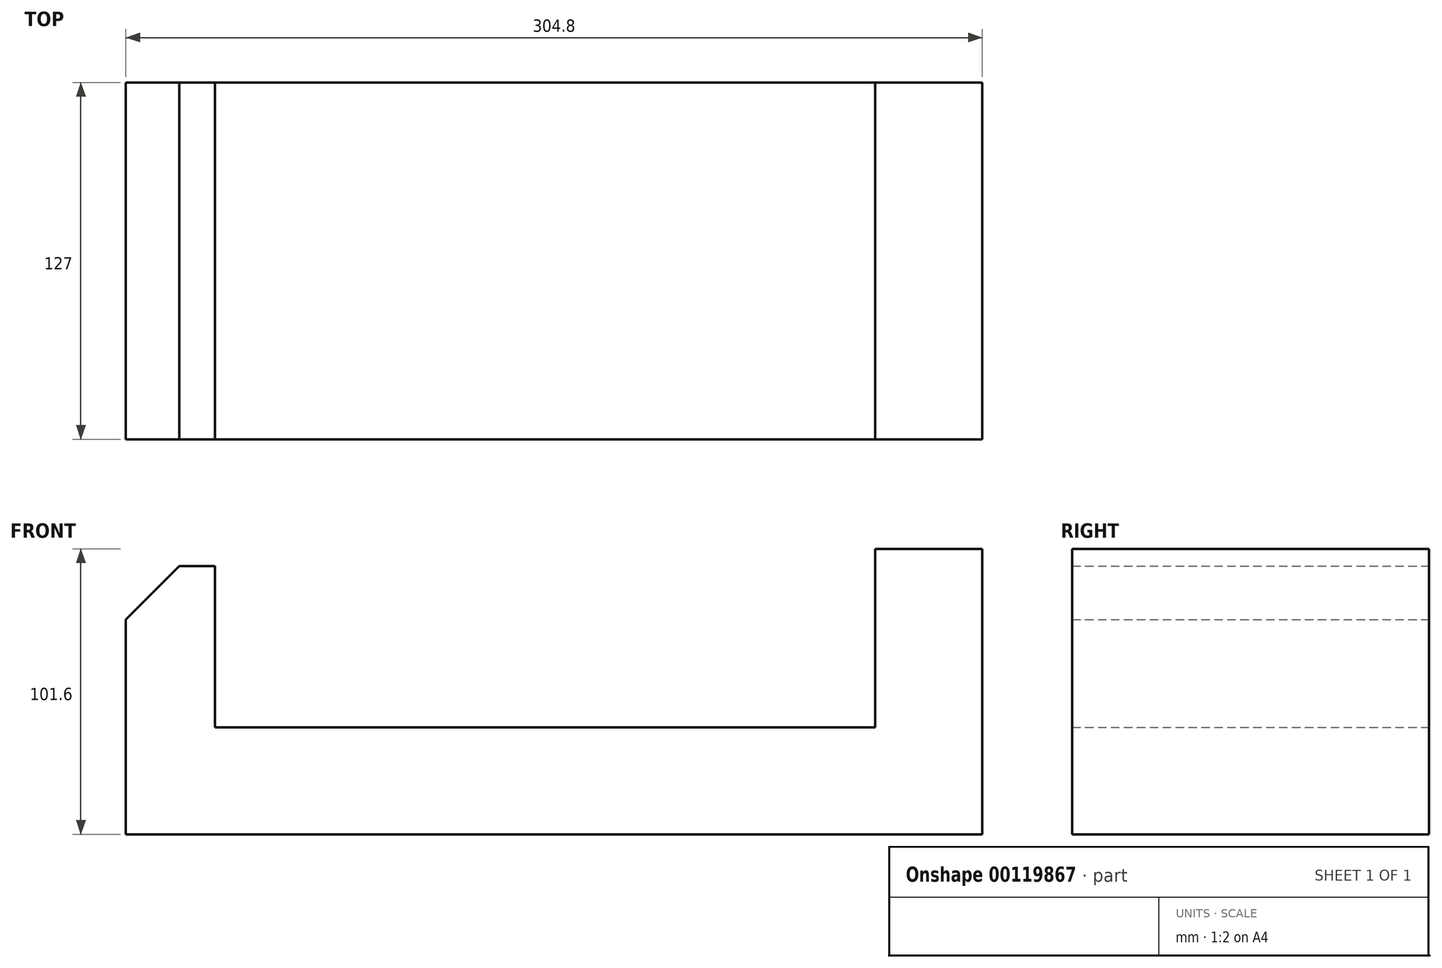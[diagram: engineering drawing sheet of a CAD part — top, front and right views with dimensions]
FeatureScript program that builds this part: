
annotation { "Feature Type Name" : "Feature", "Feature Type Description" : "" }
export const myFeature = defineFeature(function(context is Context, id is Id, definition is map)
    precondition{}
    {
        {
            var Q0;
            Q0=qCreatedBy(makeId("Front.planeOp"),FACE);
            var sketch = newSketch(context, id + "F0", { "sketchPlane" : qUnion([Q0])});
            skLineSegment(sketch, "E0", {"start": v(0, 0) * mm, "end": v(304.8, 0) * mm});
            skLineSegment(sketch, "E1", {"start": v(304.8, 0) * mm, "end": v(304.8, 101.6) * mm});
            skLineSegment(sketch, "E2", {"start": v(304.8, 101.6) * mm, "end": v(266.7, 101.6) * mm});
            skLineSegment(sketch, "E3", {"start": v(266.7, 101.6) * mm, "end": v(266.7, 38.1) * mm});
            skLineSegment(sketch, "E4", {"start": v(266.7, 38.1) * mm, "end": v(31.75, 38.1) * mm});
            skLineSegment(sketch, "E5", {"start": v(31.75, 38.1) * mm, "end": v(31.75, 95.46) * mm});
            skLineSegment(sketch, "E6", {"start": v(31.75, 95.46) * mm, "end": v(0, 95.46) * mm});
            skLineSegment(sketch, "E7", {"start": v(0, 95.46) * mm, "end": v(0, -3.93) * mm});
            skLineSegment(sketch, "E8", {"start": v(266.7, 50.8) * mm, "end": v(304.8, 50.8) * mm});
            skSolve(sketch);
        }
        {
            var Q0;
            {var subQ0=sQuery(id+"F0.wireOp",EDGE,"E2");Q0=makeQuery(id+"F0.imprint","IMPRINT",FACE,{"disambiguationData":[TD([[makeQuery(id+"F0.imprint","IMPRINT",EDGE,{"derivedFrom":subQ0}),1.0]])]});}
            var Q1;
            {var subQ4=sQuery(id+"F0.wireOp",EDGE,"E0");Q1=makeQuery(id+"F0.imprint","IMPRINT",FACE,{"disambiguationData":[TD([[makeQuery(id+"F0.imprint","IMPRINT",EDGE,{"derivedFrom":subQ4}),1.0]])]});}
            extrude(context, id + "F1", {"entities" : qUnion([Q0, Q1]), "depth" : 127 * mm});
        }
        {
            var Q0;
            Q0=makeQuery(id+"F1.opExtrude","SWEPT_EDGE",EDGE,{"disambiguationData":[OSD([sQuery(id+"F0.wireOp",EDGE,"E6"),sQuery(id+"F0.wireOp",EDGE,"E7")])]});
            chamfer(context, id + "F2", {"entities" : qUnion([Q0]), "chamferType" : ChamferType.TWO_OFFSETS, "width1" : 19.05 * mm, "oppositeDirection" : false, "width2" : 19.05 * mm, "tangentPropagation" : true});
        }
    });
